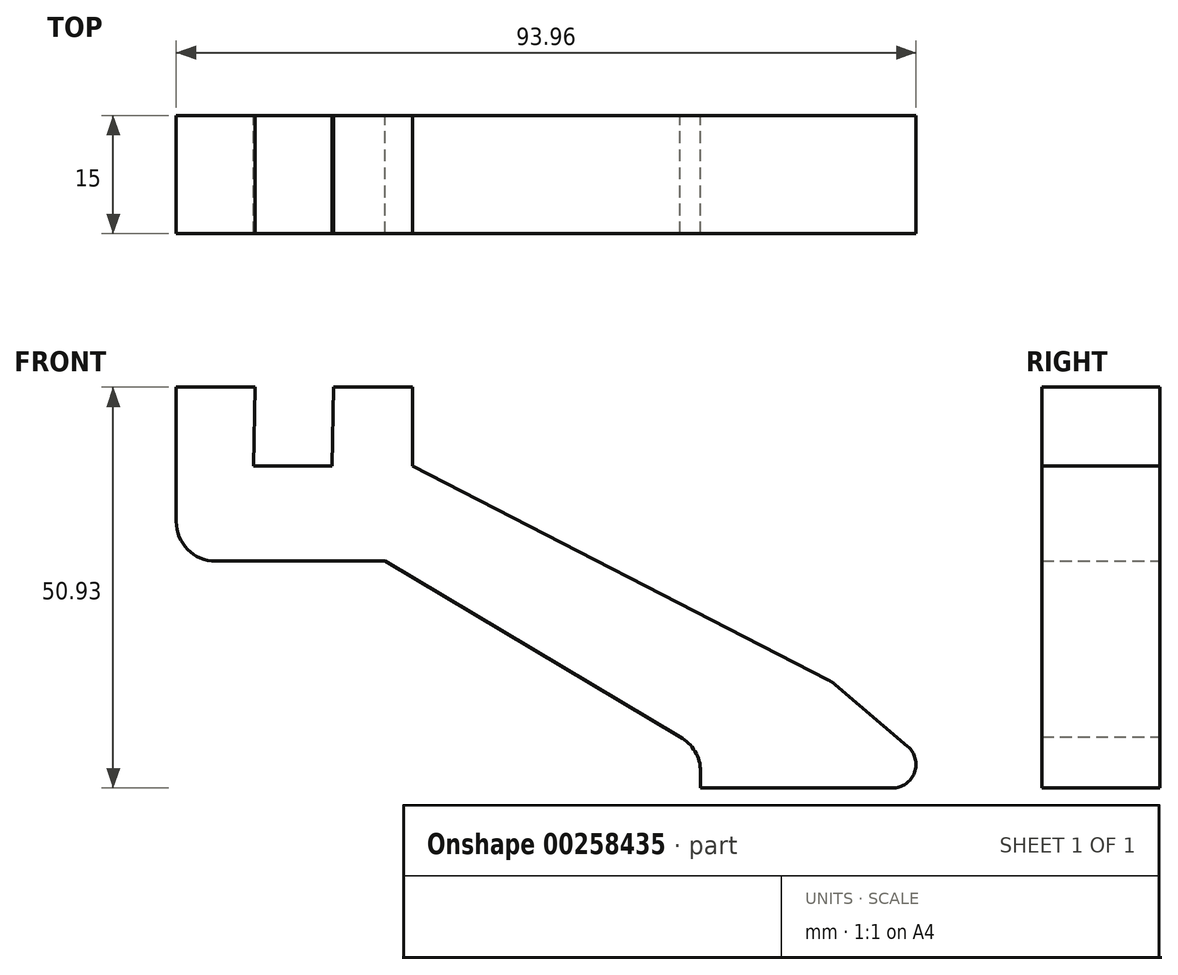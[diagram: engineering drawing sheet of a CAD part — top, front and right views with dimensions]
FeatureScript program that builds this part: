
annotation { "Feature Type Name" : "Feature", "Feature Type Description" : "" }
export const myFeature = defineFeature(function(context is Context, id is Id, definition is map)
    precondition{}
    {
        {
            var Q0;
            Q0=qCreatedBy(makeId("Front.planeOp"),FACE);
            var sketch = newSketch(context, id + "F0", { "sketchPlane" : qUnion([Q0])});
            skLineSegment(sketch, "E0", {"start": v(12.96, 0) * mm, "end": v(65.75, -27.2) * mm});
            skLineSegment(sketch, "E1", {"start": v(66.7, -27.83) * mm, "end": v(75.87, -35.64) * mm});
            skLineSegment(sketch, "E2", {"start": v(73.92, -40.93) * mm, "end": v(49.56, -40.93) * mm});
            skLineSegment(sketch, "E3", {"start": v(49.56, -40.93) * mm, "end": v(49.56, -38.84) * mm});
            skPoint(sketch, "E4.visualSharp", {"position": v(66.26, -27.46) * mm});
            skArc(sketch, "E4.filletArc", {"start": v(66.7, -27.83) * mm, "mid": v(66.24, -27.49) * mm, "end": v(65.75, -27.2) * mm});
            skPoint(sketch, "E5.visualSharp", {"position": v(49.56, -35.87) * mm});
            skArc(sketch, "E5.filletArc", {"start": v(49.56, -38.84) * mm, "mid": v(48.86, -36.29) * mm, "end": v(46.95, -34.45) * mm});
            skLineSegment(sketch, "E6.bottom", {"start": v(-7.22, 0) * mm, "end": v(2.78, 0) * mm});
            skLineSegment(sketch, "E6.left", {"start": v(-7.22, 0) * mm, "end": v(-7.04, 10) * mm});
            skLineSegment(sketch, "E6.right", {"start": v(2.78, 0) * mm, "end": v(2.96, 10) * mm});
            skLineSegment(sketch, "E7", {"start": v(-17.04, 0) * mm, "end": v(-17.04, 10) * mm});
            skLineSegment(sketch, "E8", {"start": v(-17.04, 10) * mm, "end": v(-7.04, 10) * mm});
            skLineSegment(sketch, "E9", {"start": v(2.96, 10) * mm, "end": v(12.96, 10) * mm});
            skLineSegment(sketch, "E10", {"start": v(12.96, 10) * mm, "end": v(12.96, 0) * mm});
            skLineSegment(sketch, "E11", {"start": v(-17.04, 0) * mm, "end": v(-17.04, -12.1) * mm});
            skLineSegment(sketch, "E12", {"start": v(-17.04, -12.1) * mm, "end": v(9.5, -12.1) * mm});
            skLineSegment(sketch, "E13", {"start": v(9.5, -12.1) * mm, "end": v(46.95, -34.45) * mm});
            skPoint(sketch, "E14.visualSharp", {"position": v(82.07, -40.93) * mm});
            skArc(sketch, "E14.filletArc", {"start": v(73.92, -40.93) * mm, "mid": v(76.74, -38.96) * mm, "end": v(75.87, -35.64) * mm});
            skSolve(sketch);
        }
        {
            var Q0;
            Q0 = qSketchRegion(id + "F0", true);
            extrude(context, id + "F1", {"entities" : qUnion([Q0]), "depth" : 15 * mm});
        }
        {
            var Q0;
            Q0=makeQuery(id+"F1.opExtrude","SWEPT_EDGE",EDGE,{"disambiguationData":[OSD([sQuery(id+"F0.wireOp",EDGE,"E11"),sQuery(id+"F0.wireOp",EDGE,"E12")])]});
            fillet(context, id + "F2", {"entities" : qUnion([Q0]), "radius" : 5 * mm, "tangentPropagation" : true, "allowEdgeOverflow" : false});
        }
    });
